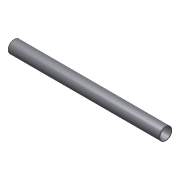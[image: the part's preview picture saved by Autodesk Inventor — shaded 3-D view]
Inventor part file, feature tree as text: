
AUTODESK INVENTOR PART (.ipt)
format: ipt  version: 2012 (Build 160160000, 160)  size: 110,080 bytes
history: native  units: in
note: dims shown in document units (in); Inventor stores cm internally (conversion verified against a paired STEP export)
features: other x42, revolve x1, sketch x1
ambient origin geometry x8: Origin, YZ Plane, XZ Plane, XY Plane, X Axis, Y Axis, Z Axis, Center Point
bodies: Solid1 (feature_tree)
feature tree (44):
  revolve  "Revolution1"  [1 undecoded]
  other  "tube_front_XY"
  other  "tube_front_YZ"
  other  "tube_front_ZX"
  other  "tube_front_X"
  other  "tube_front_Y"
  other  "tube_front_Z"
  other  "tube_front_Center"
  other  "tube_rear_XY"
  other  "tube_rear_YZ"
  other  "tube_rear_ZX"
  other  "tube_rear_X"
  other  "tube_rear_Y"
  other  "tube_rear_Z"
  other  "tube_rear_Center"
  other  "cp1_XY"
  other  "cp1_YZ"
  other  "cp1_ZX"
  other  "cp1_X"
  other  "cp1_Y"
  other  "cp1_Z"
  other  "cp1_Center"
  other  "cp2_XY"
  other  "cp2_YZ"
  other  "cp2_ZX"
  other  "cp2_X"
  other  "cp2_Y"
  other  "cp2_Z"
  other  "cp2_Center"
  other  "cp3_XY"
  other  "cp3_YZ"
  other  "cp3_ZX"
  other  "cp3_X"
  other  "cp3_Y"
  other  "cp3_Z"
  other  "cp3_Center"
  other  "cp4_XY"
  other  "cp4_YZ"
  other  "cp4_ZX"
  other  "cp4_X"
  other  "cp4_Y"
  other  "cp4_Z"
  other  "cp4_Center"
  sketch  "Sketch_1"  dims[d0=360.0deg]
note: 1 required parameter value undecoded (feature->parameter linkage not recoverable at this tier; creation-order binding heuristic only, values carry confidence <= 0.55)
